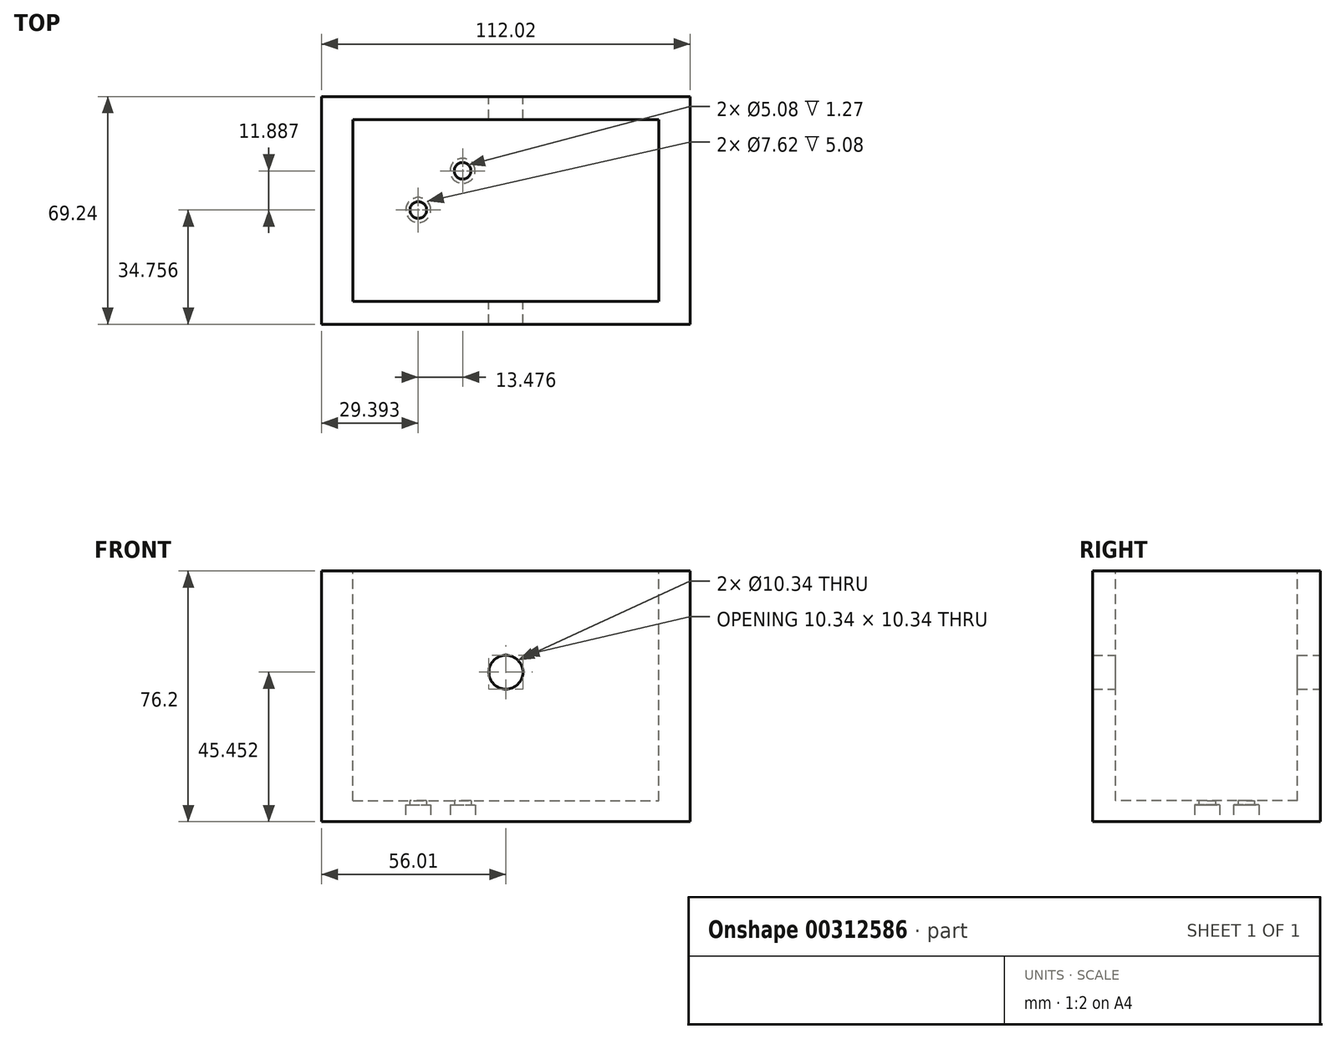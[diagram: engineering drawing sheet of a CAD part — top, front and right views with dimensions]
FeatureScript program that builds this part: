
annotation { "Feature Type Name" : "Feature", "Feature Type Description" : "" }
export const myFeature = defineFeature(function(context is Context, id is Id, definition is map)
    precondition{}
    {
        {
            var Q0;
            Q0=qCreatedBy(makeId("Top.planeOp"),FACE);
            var sketch = newSketch(context, id + "F0", { "sketchPlane" : qUnion([Q0])});
            skLineSegment(sketch, "E0.bottom", {"start": v(-38.1, 50.8) * mm, "end": v(38.1, 50.8) * mm});
            skLineSegment(sketch, "E0.top", {"start": v(-38.1, -50.8) * mm, "end": v(38.1, -50.8) * mm});
            skLineSegment(sketch, "E0.left", {"start": v(-38.1, 50.8) * mm, "end": v(-38.1, -50.8) * mm});
            skLineSegment(sketch, "E0.right", {"start": v(38.1, 50.8) * mm, "end": v(38.1, -50.8) * mm});
            skPoint(sketch, "E0.middle", {"position": v(0, 0) * mm});
            skSolve(sketch);
        }
        {
            var Q0;
            Q0=qCreatedBy(makeId("Top.planeOp"),FACE);
            var sketch = newSketch(context, id + "F1", { "sketchPlane" : qUnion([Q0])});
            skLineSegment(sketch, "E1.bottom", {"start": v(-56, -34.62) * mm, "end": v(56, -34.62) * mm});
            skLineSegment(sketch, "E1.top", {"start": v(-56, 34.62) * mm, "end": v(56, 34.62) * mm});
            skLineSegment(sketch, "E1.left", {"start": v(-56, -34.62) * mm, "end": v(-56, 34.62) * mm});
            skLineSegment(sketch, "E1.right", {"start": v(56, -34.62) * mm, "end": v(56, 34.62) * mm});
            skPoint(sketch, "E1.middle", {"position": v(0, 0) * mm});
            skSolve(sketch);
        }
        {
            var Q0;
            Q0=makeQuery(id+"F1.imprint","IMPRINT",FACE,{"disambiguationData":[TD([[makeQuery(id+"F1.imprint","IMPRINT",EDGE,{"derivedFrom":sQuery(id+"F1.wireOp",EDGE,"E1.bottom")}),1.0]])]});
            extrude(context, id + "F2", {"entities" : qUnion([Q0]), "depth" : 76.2 * mm});
        }
        {
            var Q0;
            Q0=makeQuery(id+"F2.opExtrude","CAP_FACE",FACE,{"disambiguationData":[OSD([sQuery(id+"F1.wireOp",EDGE,"E1.bottom"),sQuery(id+"F1.wireOp",EDGE,"E1.top"),sQuery(id+"F1.wireOp",EDGE,"E1.left"),sQuery(id+"F1.wireOp",EDGE,"E1.right")])],"isStart":false});
            var sketch = newSketch(context, id + "F3", { "sketchPlane" : qUnion([Q0])});
            skLineSegment(sketch, "E2.bottom", {"start": v(-46.47, 27.63) * mm, "end": v(46.47, 27.63) * mm});
            skLineSegment(sketch, "E2.top", {"start": v(-46.47, -27.63) * mm, "end": v(46.47, -27.63) * mm});
            skLineSegment(sketch, "E2.left", {"start": v(-46.47, 27.63) * mm, "end": v(-46.47, -27.63) * mm});
            skLineSegment(sketch, "E2.right", {"start": v(46.47, 27.63) * mm, "end": v(46.47, -27.63) * mm});
            skPoint(sketch, "E2.middle", {"position": v(0, 0) * mm});
            skSolve(sketch);
        }
        {
            var Q0;
            Q0=makeQuery(id+"F3.imprint","IMPRINT",FACE,{"disambiguationData":[TD([[makeQuery(id+"F3.imprint","IMPRINT",EDGE,{"derivedFrom":sQuery(id+"F3.wireOp",EDGE,"E2.bottom")}),-1.0]])]});
            var sketch = newSketch(context, id + "F4", { "sketchPlane" : qUnion([Q0])});
            skSolve(sketch);
        }
        {
            var Q0;
            Q0=makeQuery(id+"F4.imprint","IMPRINT",FACE,{"disambiguationData":[TD([[makeQuery(id+"F4.imprint","IMPRINT",EDGE,{"derivedFrom":makeQuery(id+"F3.imprint","IMPRINT",EDGE,{"derivedFrom":sQuery(id+"F3.wireOp",EDGE,"E2.bottom")})}),-1.0]])]});
            extrude(context, id + "F5", {"entities" : qUnion([Q0]), "operationType" : NewBodyOperationType.REMOVE, "oppositeDirection" : true, "depth" : 69.85 * mm});
        }
        {
            var Q0;
            Q0=makeQuery(id+"F2.opExtrude","SWEPT_FACE",FACE,{"disambiguationData":[OSD([sQuery(id+"F1.wireOp",EDGE,"E1.top")])]});
            var sketch = newSketch(context, id + "F6", { "sketchPlane" : qUnion([Q0])});
            skSolve(sketch);
        }
        {
            var Q0;
            {var subQ0=sQuery(id+"F1.wireOp",EDGE,"E1.top");Q0=makeQuery(id+"F6.imprint","IMPRINT",FACE,{"disambiguationData":[TD([[makeQuery(id+"F6.imprint","IMPRINT",EDGE,{"derivedFrom":makeQuery(id+"F2.opExtrude","CAP_EDGE",EDGE,{"disambiguationData":[OSD([subQ0])],"isStart":true})}),-1.0]])]});}
            var sketch = newSketch(context, id + "F7", { "sketchPlane" : qUnion([Q0])});
            skPoint(sketch, "E3", {"position": v(0, 76.2) * mm});
            skPoint(sketch, "E4", {"position": v(0, 15.16) * mm});
            skSolve(sketch);
        }
        {
            var Q0;
            {var subQ0=sQuery(id+"F1.wireOp",EDGE,"E1.top");Q0=makeQuery(id+"F6.imprint","IMPRINT",FACE,{"disambiguationData":[TD([[makeQuery(id+"F6.imprint","IMPRINT",EDGE,{"derivedFrom":makeQuery(id+"F2.opExtrude","CAP_EDGE",EDGE,{"disambiguationData":[OSD([subQ0])],"isStart":true})}),-1.0]])]});}
            var sketch = newSketch(context, id + "F8", { "sketchPlane" : qUnion([Q0])});
            skLineSegment(sketch, "E5", {"start": v(0, 76.1) * mm, "end": v(0, 14.81) * mm});
            skCircle(sketch, "E6", {"center": v(0, 45.45) * mm, "radius": 3.81 * mm});
            skSolve(sketch);
        }
        {
            var Q0;
            Q0=sQuery(id+"F8.wireOp",VERTEX,"E6.center");
            var Q1;
            Q1=makeQuery(id+"F2.opExtrude","SWEPT_BODY",BODY,{"disambiguationData":[OSD([sQuery(id+"F1.wireOp",EDGE,"E1.bottom"),sQuery(id+"F1.wireOp",EDGE,"E1.top"),sQuery(id+"F1.wireOp",EDGE,"E1.left"),sQuery(id+"F1.wireOp",EDGE,"E1.right")])]});
            hole(context, id + "F9", {"style" : HoleStyle.SIMPLE, "endStyle" : HoleEndStyle.THROUGH, "holeDiameter" : 10.34 * mm, "tappedDepth" : 12.7 * mm, "tapClearance" : 3, "locations" : qUnion([Q0]), "scope" : qUnion([Q1])});
        }
        {
            var Q0;
            Q0=makeQuery(id+"F0.imprint","IMPRINT",FACE,{"disambiguationData":[TD([[makeQuery(id+"F0.imprint","IMPRINT",EDGE,{"derivedFrom":sQuery(id+"F0.wireOp",EDGE,"E0.bottom")}),-1.0]])]});
            var sketch = newSketch(context, id + "F10", { "sketchPlane" : qUnion([Q0])});
            skCircle(sketch, "E7", {"center": v(-26.62, 0.14) * mm, "radius": 8.9 * mm});
            skPoint(sketch, "E7.first.point", {"position": v(-17.73, 0) * mm});
            skPoint(sketch, "E7.second.point", {"position": v(-35.5, 0) * mm});
            skPoint(sketch, "E7.third.point", {"position": v(-30.3, -7.96) * mm});
            skSolve(sketch);
        }
        {
            var Q0;
            Q0=makeQuery(id+"F0.imprint","IMPRINT",FACE,{"disambiguationData":[TD([[makeQuery(id+"F0.imprint","IMPRINT",EDGE,{"derivedFrom":sQuery(id+"F0.wireOp",EDGE,"E0.bottom")}),-1.0]])]});
            var sketch = newSketch(context, id + "F11", { "sketchPlane" : qUnion([Q0])});
            skCircle(sketch, "E8", {"center": v(-13.14, 12.02) * mm, "radius": 8.9 * mm});
            skPoint(sketch, "E8.first.point", {"position": v(-17.07, 20) * mm});
            skSolve(sketch);
        }
        {
            var Q0;
            Q0=sQuery(id+"F3.wireOp",EDGE,"E2.top");
            var Q1;
            Q1=sQuery(id+"F3.wireOp",EDGE,"E2.left");
            var Q2;
            Q2=sQuery(id+"F3.wireOp",EDGE,"E2.bottom");
            var Q3;
            Q3=sQuery(id+"F3.wireOp",EDGE,"E2.right");
            extrude(context, id + "F13", {"bodyType" : ToolBodyType.SURFACE, "surfaceEntities" : qUnion([Q0, Q1, Q2, Q3]), "oppositeDirection" : true, "depth" : 69.85 * mm});
        }
        {
            var Q0;
            Q0=sQuery(id+"F11.wireOp",VERTEX,"E8.center");
            var Q1;
            Q1=makeQuery(id+"F2.opExtrude","SWEPT_BODY",BODY,{"disambiguationData":[OSD([sQuery(id+"F1.wireOp",EDGE,"E1.bottom"),sQuery(id+"F1.wireOp",EDGE,"E1.top"),sQuery(id+"F1.wireOp",EDGE,"E1.left"),sQuery(id+"F1.wireOp",EDGE,"E1.right")])]});
            hole(context, id + "F15", {"style" : HoleStyle.C_BORE, "endStyle" : HoleEndStyle.BLIND, "oppositeDirection" : true, "holeDiameter" : 5.08 * mm, "cBoreDiameter" : 7.62 * mm, "cBoreDepth" : 5.08 * mm, "holeDepth" : 12.7 * mm, "tappedDepth" : 12.7 * mm, "tapClearance" : 3, "locations" : qUnion([Q0]), "scope" : qUnion([Q1])});
        }
        {
            var Q0;
            Q0=sQuery(id+"F10.wireOp",VERTEX,"E7.center");
            var Q1;
            Q1=makeQuery(id+"F2.opExtrude","SWEPT_BODY",BODY,{"disambiguationData":[OSD([sQuery(id+"F1.wireOp",EDGE,"E1.bottom"),sQuery(id+"F1.wireOp",EDGE,"E1.top"),sQuery(id+"F1.wireOp",EDGE,"E1.left"),sQuery(id+"F1.wireOp",EDGE,"E1.right")])]});
            hole(context, id + "F16", {"style" : HoleStyle.C_BORE, "endStyle" : HoleEndStyle.BLIND, "oppositeDirection" : true, "holeDiameter" : 5.08 * mm, "cBoreDiameter" : 7.62 * mm, "cBoreDepth" : 5.08 * mm, "holeDepth" : 12.7 * mm, "tappedDepth" : 12.7 * mm, "tapClearance" : 3, "locations" : qUnion([Q0]), "scope" : qUnion([Q1])});
        }
    });
